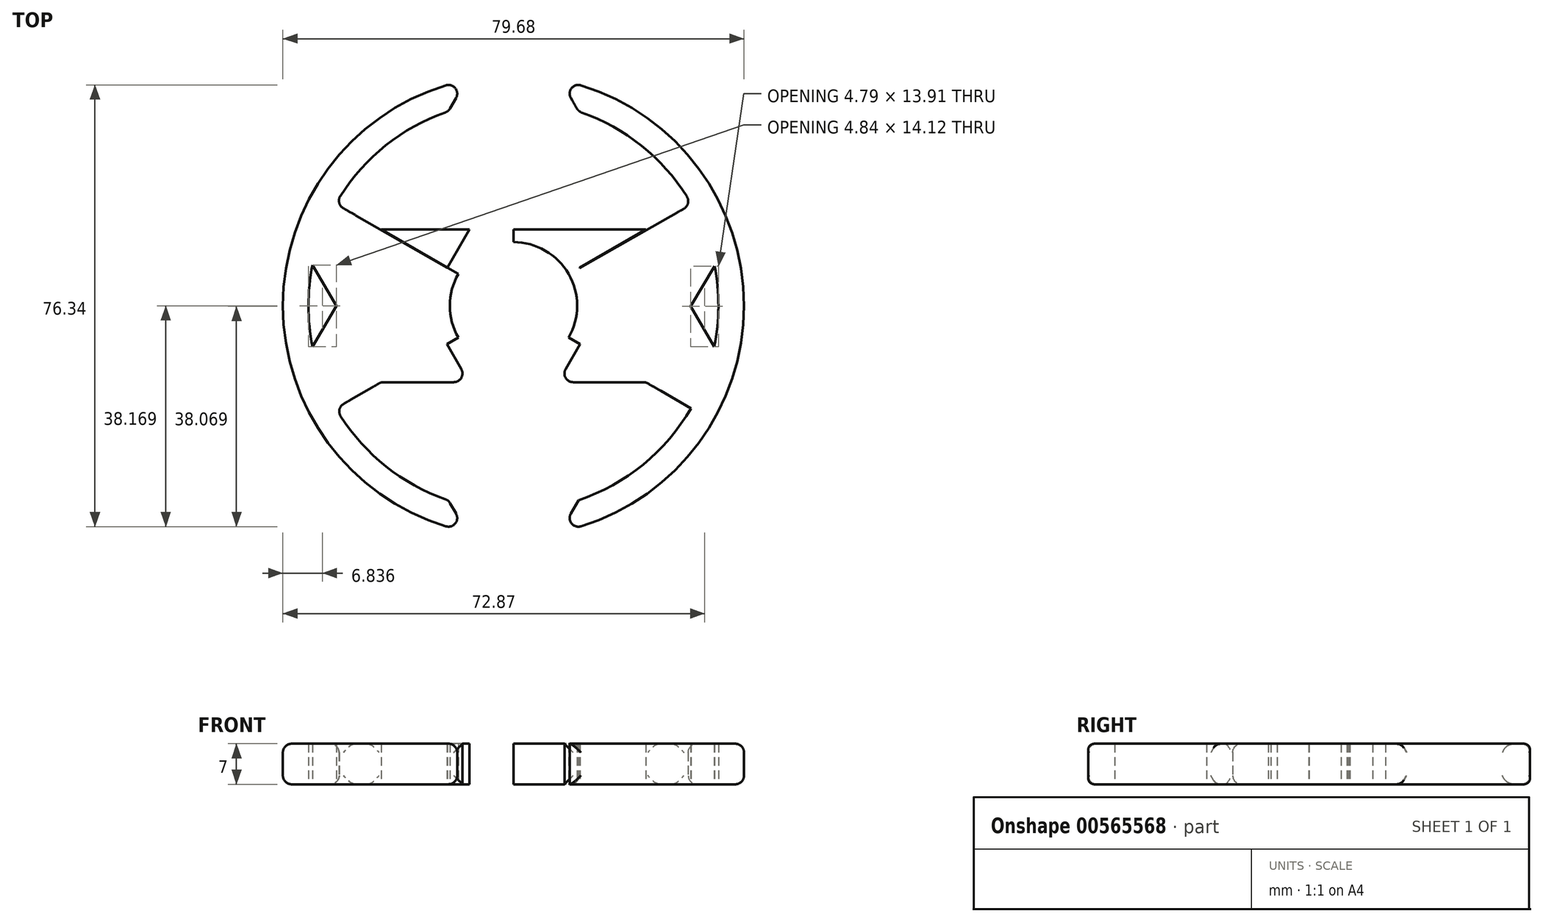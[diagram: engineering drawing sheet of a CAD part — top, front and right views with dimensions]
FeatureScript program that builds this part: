
annotation { "Feature Type Name" : "Feature", "Feature Type Description" : "" }
export const myFeature = defineFeature(function(context is Context, id is Id, definition is map)
    precondition{}
    {
        {
            var Q0;
            Q0=qCreatedBy(makeId("Top.planeOp"),FACE);
            var sketch = newSketch(context, id + "F0", { "sketchPlane" : qUnion([Q0])});
            skCircle(sketch, "E0", {"center": v(0, 0) * mm, "radius": 11 * mm});
            skCircle(sketch, "E1", {"center": v(0, 0) * mm, "radius": 26.4 * mm});
            skLineSegment(sketch, "E2", {"start": v(0, 0) * mm, "end": v(0, 26.4) * mm});
            skLineSegment(sketch, "E3", {"start": v(0, 0) * mm, "end": v(22.86, -13.2) * mm});
            skLineSegment(sketch, "E4", {"start": v(0, 0) * mm, "end": v(-22.86, -13.2) * mm});
            skLineSegment(sketch, "E5", {"start": v(0, 26.4) * mm, "end": v(-22.86, -13.2) * mm});
            skLineSegment(sketch, "E6", {"start": v(-22.86, -13.2) * mm, "end": v(22.86, -13.2) * mm});
            skLineSegment(sketch, "E7", {"start": v(22.86, -13.2) * mm, "end": v(0, 26.4) * mm});
            skCircle(sketch, "E8", {"center": v(0, 0) * mm, "radius": 30.74 * mm});
            skCircle(sketch, "E9", {"center": v(0, 0) * mm, "radius": 35.42 * mm});
            skCircle(sketch, "E10", {"center": v(0, 0) * mm, "radius": 39.84 * mm});
            skCircle(sketch, "E11", {"center": v(0, 0) * mm, "radius": 43.95 * mm});
            skCircle(sketch, "E12", {"center": v(0, 0) * mm, "radius": 48.64 * mm});
            skCircle(sketch, "E13", {"center": v(0, 0) * mm, "radius": 53.34 * mm});
            skLineSegment(sketch, "E14", {"start": v(0, 0) * mm, "end": v(-46.19, -26.67) * mm});
            skLineSegment(sketch, "E15", {"start": v(0, 0) * mm, "end": v(46.19, -26.67) * mm});
            skLineSegment(sketch, "E16", {"start": v(0, 0) * mm, "end": v(0, 53.34) * mm});
            skLineSegment(sketch, "E17", {"start": v(0, 0) * mm, "end": v(0, -26.67) * mm});
            skLineSegment(sketch, "E18", {"start": v(0, 0) * mm, "end": v(22.86, 13.2) * mm});
            skLineSegment(sketch, "E19", {"start": v(0, 0) * mm, "end": v(-22.86, 13.2) * mm});
            skLineSegment(sketch, "E20", {"start": v(-22.86, 13.2) * mm, "end": v(0, -26.67) * mm});
            skLineSegment(sketch, "E21", {"start": v(22.86, 13.2) * mm, "end": v(0, -26.67) * mm});
            skLineSegment(sketch, "E22", {"start": v(-22.86, 13.2) * mm, "end": v(22.86, 13.2) * mm});
            skLineSegment(sketch, "E23", {"start": v(0, 0) * mm, "end": v(46.35, 26.4) * mm});
            skLineSegment(sketch, "E24", {"start": v(0, 0) * mm, "end": v(0, -53.34) * mm});
            skLineSegment(sketch, "E25", {"start": v(0, 0) * mm, "end": v(-46.03, 26.4) * mm});
            skLineSegment(sketch, "E26", {"start": v(-46.03, 26.4) * mm, "end": v(-22.86, -13.2) * mm});
            skLineSegment(sketch, "E27", {"start": v(-46.19, -26.67) * mm, "end": v(-22.86, 13.2) * mm});
            skLineSegment(sketch, "E28", {"start": v(-46.19, -26.67) * mm, "end": v(0, -26.67) * mm});
            skLineSegment(sketch, "E29", {"start": v(-22.86, -13.2) * mm, "end": v(0, -53.34) * mm});
            skLineSegment(sketch, "E30", {"start": v(22.86, -13.2) * mm, "end": v(0, -53.34) * mm});
            skLineSegment(sketch, "E31", {"start": v(46.19, -26.67) * mm, "end": v(0, -26.67) * mm});
            skLineSegment(sketch, "E32", {"start": v(22.86, 13.2) * mm, "end": v(46.19, -26.67) * mm});
            skLineSegment(sketch, "E33", {"start": v(46.35, 26.4) * mm, "end": v(22.86, -13.2) * mm});
            skLineSegment(sketch, "E34", {"start": v(0, 26.4) * mm, "end": v(46.35, 26.4) * mm});
            skLineSegment(sketch, "E35", {"start": v(0, 53.34) * mm, "end": v(22.86, 13.2) * mm});
            skLineSegment(sketch, "E36", {"start": v(0, 53.34) * mm, "end": v(-22.86, 13.2) * mm});
            skLineSegment(sketch, "E37", {"start": v(-46.03, 26.4) * mm, "end": v(0, 26.4) * mm});
            skSolve(sketch);
        }
        {
            var Q0;
            {var subQ5=sQuery(id+"F0.wireOp",EDGE,"E0");var subQ7=sQuery(id+"F0.wireOp",EDGE,"E25");var subQ9=makeQuery(id+"F0.imprint","INTERSECT",VERTEX,{"derivedFrom":[subQ5,subQ7]});Q0=makeQuery(id+"F0.imprint","IMPRINT",FACE,{"disambiguationData":[TD([[makeQuery(id+"F0.imprint","IMPRINT",EDGE,{"disambiguationData":[TD([[subQ9,-1.0]])],"derivedFrom":subQ5}),-1.0]])]});}
            var Q1;
            {var subQ5=sQuery(id+"F0.wireOp",EDGE,"E23");var subQ7=sQuery(id+"F0.wireOp",EDGE,"E0");var subQ9=makeQuery(id+"F0.imprint","INTERSECT",VERTEX,{"derivedFrom":[subQ7,subQ5]});Q1=makeQuery(id+"F0.imprint","IMPRINT",FACE,{"disambiguationData":[TD([[makeQuery(id+"F0.imprint","IMPRINT",EDGE,{"disambiguationData":[TD([[subQ9,1.0]])],"derivedFrom":subQ7}),-1.0]])]});}
            var Q2;
            {var subQ3=sQuery(id+"F0.wireOp",EDGE,"E14");var subQ5=sQuery(id+"F0.wireOp",EDGE,"E0");var subQ6=makeQuery(id+"F0.imprint","INTERSECT",VERTEX,{"derivedFrom":[subQ5,subQ3]});Q2=makeQuery(id+"F0.imprint","IMPRINT",FACE,{"disambiguationData":[TD([[makeQuery(id+"F0.imprint","IMPRINT",EDGE,{"disambiguationData":[TD([[subQ6,-1.0]])],"derivedFrom":subQ5}),-1.0]])]});}
            var Q3;
            {var subQ0=sQuery(id+"F0.wireOp",EDGE,"E18");var subQ1=sQuery(id+"F0.wireOp",EDGE,"E0");var subQ2=makeQuery(id+"F0.imprint","INTERSECT",VERTEX,{"derivedFrom":[subQ1,subQ0]});Q3=makeQuery(id+"F0.imprint","IMPRINT",FACE,{"disambiguationData":[TD([[makeQuery(id+"F0.imprint","IMPRINT",EDGE,{"disambiguationData":[TD([[subQ2,-1.0]])],"derivedFrom":subQ1}),-1.0]])]});}
            var Q4;
            {var subQ5=sQuery(id+"F0.wireOp",EDGE,"E0");var subQ7=sQuery(id+"F0.wireOp",EDGE,"E24");var subQ9=makeQuery(id+"F0.imprint","INTERSECT",VERTEX,{"derivedFrom":[subQ5,subQ7]});Q4=makeQuery(id+"F0.imprint","IMPRINT",FACE,{"disambiguationData":[TD([[makeQuery(id+"F0.imprint","IMPRINT",EDGE,{"disambiguationData":[TD([[subQ9,-1.0]])],"derivedFrom":subQ5}),-1.0]])]});}
            var Q5;
            {var subQ1=sQuery(id+"F0.wireOp",EDGE,"E0");var subQ5=sQuery(id+"F0.wireOp",EDGE,"E16");var subQ6=makeQuery(id+"F0.imprint","INTERSECT",VERTEX,{"derivedFrom":[subQ1,subQ5]});Q5=makeQuery(id+"F0.imprint","IMPRINT",FACE,{"disambiguationData":[TD([[makeQuery(id+"F0.imprint","IMPRINT",EDGE,{"disambiguationData":[TD([[subQ6,-1.0]])],"derivedFrom":subQ1}),-1.0]])]});}
            var Q6;
            {var subQ0=sQuery(id+"F0.wireOp",EDGE,"E25");var subQ1=sQuery(id+"F0.wireOp",EDGE,"E5");var subQ2=makeQuery(id+"F0.imprint","INTERSECT",VERTEX,{"derivedFrom":[subQ1,subQ0]});Q6=makeQuery(id+"F0.imprint","IMPRINT",FACE,{"disambiguationData":[TD([[makeQuery(id+"F0.imprint","IMPRINT",EDGE,{"disambiguationData":[TD([[subQ2,-1.0]])],"derivedFrom":subQ1}),-1.0]])]});}
            var Q7;
            {var subQ1=sQuery(id+"F0.wireOp",EDGE,"E5");var subQ3=sQuery(id+"F0.wireOp",EDGE,"E20");var subQ4=makeQuery(id+"F0.imprint","INTERSECT",VERTEX,{"derivedFrom":[subQ1,subQ3]});Q7=makeQuery(id+"F0.imprint","IMPRINT",FACE,{"disambiguationData":[TD([[makeQuery(id+"F0.imprint","IMPRINT",EDGE,{"disambiguationData":[TD([[subQ4,-1.0]])],"derivedFrom":subQ3}),-1.0]])]});}
            var Q8;
            {var subQ0=sQuery(id+"F0.wireOp",EDGE,"E5");var subQ5=sQuery(id+"F0.wireOp",EDGE,"E20");var subQ6=makeQuery(id+"F0.imprint","INTERSECT",VERTEX,{"derivedFrom":[subQ0,subQ5]});Q8=makeQuery(id+"F0.imprint","IMPRINT",FACE,{"disambiguationData":[TD([[makeQuery(id+"F0.imprint","IMPRINT",EDGE,{"disambiguationData":[TD([[subQ6,1.0]])],"derivedFrom":subQ5}),-1.0]])]});}
            var Q9;
            {var subQ0=sQuery(id+"F0.wireOp",EDGE,"E7");var subQ5=sQuery(id+"F0.wireOp",EDGE,"E21");var subQ6=makeQuery(id+"F0.imprint","INTERSECT",VERTEX,{"derivedFrom":[subQ0,subQ5]});Q9=makeQuery(id+"F0.imprint","IMPRINT",FACE,{"disambiguationData":[TD([[makeQuery(id+"F0.imprint","IMPRINT",EDGE,{"disambiguationData":[TD([[subQ6,1.0]])],"derivedFrom":subQ5}),1.0]])]});}
            var Q10;
            {var subQ0=sQuery(id+"F0.wireOp",EDGE,"E21");var subQ1=sQuery(id+"F0.wireOp",EDGE,"E7");var subQ2=makeQuery(id+"F0.imprint","INTERSECT",VERTEX,{"derivedFrom":[subQ1,subQ0]});Q10=makeQuery(id+"F0.imprint","IMPRINT",FACE,{"disambiguationData":[TD([[makeQuery(id+"F0.imprint","IMPRINT",EDGE,{"disambiguationData":[TD([[subQ2,-1.0]])],"derivedFrom":subQ1}),-1.0]])]});}
            var Q11;
            {var subQ1=sQuery(id+"F0.wireOp",EDGE,"E7");var subQ3=sQuery(id+"F0.wireOp",EDGE,"E21");var subQ4=makeQuery(id+"F0.imprint","INTERSECT",VERTEX,{"derivedFrom":[subQ1,subQ3]});Q11=makeQuery(id+"F0.imprint","IMPRINT",FACE,{"disambiguationData":[TD([[makeQuery(id+"F0.imprint","IMPRINT",EDGE,{"disambiguationData":[TD([[subQ4,-1.0]])],"derivedFrom":subQ3}),1.0]])]});}
            var Q12;
            {var subQ0=sQuery(id+"F0.wireOp",EDGE,"E22");var subQ1=sQuery(id+"F0.wireOp",EDGE,"E5");var subQ2=makeQuery(id+"F0.imprint","INTERSECT",VERTEX,{"derivedFrom":[subQ1,subQ0]});Q12=makeQuery(id+"F0.imprint","IMPRINT",FACE,{"disambiguationData":[TD([[makeQuery(id+"F0.imprint","IMPRINT",EDGE,{"disambiguationData":[TD([[subQ2,-1.0]])],"derivedFrom":subQ1}),-1.0]])]});}
            var Q13;
            {var subQ1=sQuery(id+"F0.wireOp",EDGE,"E6");var subQ3=sQuery(id+"F0.wireOp",EDGE,"E20");var subQ4=makeQuery(id+"F0.imprint","INTERSECT",VERTEX,{"derivedFrom":[subQ1,subQ3]});Q13=makeQuery(id+"F0.imprint","IMPRINT",FACE,{"disambiguationData":[TD([[makeQuery(id+"F0.imprint","IMPRINT",EDGE,{"disambiguationData":[TD([[subQ4,1.0]])],"derivedFrom":subQ3}),-1.0]])]});}
            var Q14;
            {var subQ1=sQuery(id+"F0.wireOp",EDGE,"E6");var subQ3=sQuery(id+"F0.wireOp",EDGE,"E21");var subQ4=makeQuery(id+"F0.imprint","INTERSECT",VERTEX,{"derivedFrom":[subQ1,subQ3]});Q14=makeQuery(id+"F0.imprint","IMPRINT",FACE,{"disambiguationData":[TD([[makeQuery(id+"F0.imprint","IMPRINT",EDGE,{"disambiguationData":[TD([[subQ4,1.0]])],"derivedFrom":subQ3}),1.0]])]});}
            var Q15;
            {var subQ0=sQuery(id+"F0.wireOp",EDGE,"E18");var subQ1=sQuery(id+"F0.wireOp",EDGE,"E7");var subQ2=makeQuery(id+"F0.imprint","INTERSECT",VERTEX,{"derivedFrom":[subQ1,subQ0]});Q15=makeQuery(id+"F0.imprint","IMPRINT",FACE,{"disambiguationData":[TD([[makeQuery(id+"F0.imprint","IMPRINT",EDGE,{"disambiguationData":[TD([[subQ2,-1.0]])],"derivedFrom":subQ1}),-1.0]])]});}
            var Q16;
            {var subQ0=sQuery(id+"F0.wireOp",EDGE,"E25");var subQ1=sQuery(id+"F0.wireOp",EDGE,"E8");var subQ2=makeQuery(id+"F0.imprint","INTERSECT",VERTEX,{"derivedFrom":[subQ1,subQ0]});Q16=makeQuery(id+"F0.imprint","IMPRINT",FACE,{"disambiguationData":[TD([[makeQuery(id+"F0.imprint","IMPRINT",EDGE,{"disambiguationData":[TD([[subQ2,-1.0]])],"derivedFrom":subQ1}),1.0]])]});}
            var Q17;
            {var subQ0=sQuery(id+"F0.wireOp",EDGE,"E27");var subQ1=sQuery(id+"F0.wireOp",EDGE,"E8");var subQ2=makeQuery(id+"F0.imprint","INTERSECT",VERTEX,{"derivedFrom":[subQ1,subQ0]});Q17=makeQuery(id+"F0.imprint","IMPRINT",FACE,{"disambiguationData":[TD([[makeQuery(id+"F0.imprint","IMPRINT",EDGE,{"disambiguationData":[TD([[subQ2,-1.0]])],"derivedFrom":subQ1}),1.0]])]});}
            var Q18;
            {var subQ1=sQuery(id+"F0.wireOp",EDGE,"E1");var subQ3=sQuery(id+"F0.wireOp",EDGE,"E25");var subQ4=makeQuery(id+"F0.imprint","INTERSECT",VERTEX,{"derivedFrom":[subQ1,subQ3]});Q18=makeQuery(id+"F0.imprint","IMPRINT",FACE,{"disambiguationData":[TD([[makeQuery(id+"F0.imprint","IMPRINT",EDGE,{"disambiguationData":[TD([[subQ4,-1.0]])],"derivedFrom":subQ3}),1.0]])]});}
            var Q19;
            {var subQ0=sQuery(id+"F0.wireOp",EDGE,"E23");var subQ1=sQuery(id+"F0.wireOp",EDGE,"E8");var subQ2=makeQuery(id+"F0.imprint","INTERSECT",VERTEX,{"derivedFrom":[subQ1,subQ0]});Q19=makeQuery(id+"F0.imprint","IMPRINT",FACE,{"disambiguationData":[TD([[makeQuery(id+"F0.imprint","IMPRINT",EDGE,{"disambiguationData":[TD([[subQ2,1.0]])],"derivedFrom":subQ1}),1.0]])]});}
            var Q20;
            {var subQ1=sQuery(id+"F0.wireOp",EDGE,"E1");var subQ3=sQuery(id+"F0.wireOp",EDGE,"E23");var subQ4=makeQuery(id+"F0.imprint","INTERSECT",VERTEX,{"derivedFrom":[subQ1,subQ3]});Q20=makeQuery(id+"F0.imprint","IMPRINT",FACE,{"disambiguationData":[TD([[makeQuery(id+"F0.imprint","IMPRINT",EDGE,{"disambiguationData":[TD([[subQ4,-1.0]])],"derivedFrom":subQ3}),-1.0]])]});}
            var Q21;
            {var subQ0=sQuery(id+"F0.wireOp",EDGE,"E15");var subQ1=sQuery(id+"F0.wireOp",EDGE,"E8");var subQ2=makeQuery(id+"F0.imprint","INTERSECT",VERTEX,{"derivedFrom":[subQ1,subQ0]});Q21=makeQuery(id+"F0.imprint","IMPRINT",FACE,{"disambiguationData":[TD([[makeQuery(id+"F0.imprint","IMPRINT",EDGE,{"disambiguationData":[TD([[subQ2,-1.0]])],"derivedFrom":subQ1}),1.0]])]});}
            var Q22;
            {var subQ0=sQuery(id+"F0.wireOp",EDGE,"E23");var subQ1=sQuery(id+"F0.wireOp",EDGE,"E8");var subQ2=makeQuery(id+"F0.imprint","INTERSECT",VERTEX,{"derivedFrom":[subQ1,subQ0]});Q22=makeQuery(id+"F0.imprint","IMPRINT",FACE,{"disambiguationData":[TD([[makeQuery(id+"F0.imprint","IMPRINT",EDGE,{"disambiguationData":[TD([[subQ2,1.0]])],"derivedFrom":subQ1}),-1.0]])]});}
            var Q23;
            {var subQ0=sQuery(id+"F0.wireOp",EDGE,"E23");var subQ1=sQuery(id+"F0.wireOp",EDGE,"E9");var subQ2=makeQuery(id+"F0.imprint","INTERSECT",VERTEX,{"derivedFrom":[subQ1,subQ0]});Q23=makeQuery(id+"F0.imprint","IMPRINT",FACE,{"disambiguationData":[TD([[makeQuery(id+"F0.imprint","IMPRINT",EDGE,{"disambiguationData":[TD([[subQ2,1.0]])],"derivedFrom":subQ1}),-1.0]])]});}
            var Q24;
            {var subQ0=sQuery(id+"F0.wireOp",EDGE,"E15");var subQ1=sQuery(id+"F0.wireOp",EDGE,"E9");var subQ2=makeQuery(id+"F0.imprint","INTERSECT",VERTEX,{"derivedFrom":[subQ1,subQ0]});Q24=makeQuery(id+"F0.imprint","IMPRINT",FACE,{"disambiguationData":[TD([[makeQuery(id+"F0.imprint","IMPRINT",EDGE,{"disambiguationData":[TD([[subQ2,-1.0]])],"derivedFrom":subQ1}),-1.0]])]});}
            var Q25;
            {var subQ0=sQuery(id+"F0.wireOp",EDGE,"E15");var subQ1=sQuery(id+"F0.wireOp",EDGE,"E8");var subQ2=makeQuery(id+"F0.imprint","INTERSECT",VERTEX,{"derivedFrom":[subQ1,subQ0]});Q25=makeQuery(id+"F0.imprint","IMPRINT",FACE,{"disambiguationData":[TD([[makeQuery(id+"F0.imprint","IMPRINT",EDGE,{"disambiguationData":[TD([[subQ2,-1.0]])],"derivedFrom":subQ1}),-1.0]])]});}
            var Q26;
            {var subQ0=sQuery(id+"F0.wireOp",EDGE,"E27");var subQ1=sQuery(id+"F0.wireOp",EDGE,"E8");var subQ2=makeQuery(id+"F0.imprint","INTERSECT",VERTEX,{"derivedFrom":[subQ1,subQ0]});Q26=makeQuery(id+"F0.imprint","IMPRINT",FACE,{"disambiguationData":[TD([[makeQuery(id+"F0.imprint","IMPRINT",EDGE,{"disambiguationData":[TD([[subQ2,-1.0]])],"derivedFrom":subQ1}),-1.0]])]});}
            var Q27;
            {var subQ0=sQuery(id+"F0.wireOp",EDGE,"E27");var subQ1=sQuery(id+"F0.wireOp",EDGE,"E9");var subQ2=makeQuery(id+"F0.imprint","INTERSECT",VERTEX,{"derivedFrom":[subQ1,subQ0]});Q27=makeQuery(id+"F0.imprint","IMPRINT",FACE,{"disambiguationData":[TD([[makeQuery(id+"F0.imprint","IMPRINT",EDGE,{"disambiguationData":[TD([[subQ2,-1.0]])],"derivedFrom":subQ1}),-1.0]])]});}
            var Q28;
            {var subQ0=sQuery(id+"F0.wireOp",EDGE,"E25");var subQ1=sQuery(id+"F0.wireOp",EDGE,"E9");var subQ2=makeQuery(id+"F0.imprint","INTERSECT",VERTEX,{"derivedFrom":[subQ1,subQ0]});Q28=makeQuery(id+"F0.imprint","IMPRINT",FACE,{"disambiguationData":[TD([[makeQuery(id+"F0.imprint","IMPRINT",EDGE,{"disambiguationData":[TD([[subQ2,-1.0]])],"derivedFrom":subQ1}),-1.0]])]});}
            var Q29;
            {var subQ0=sQuery(id+"F0.wireOp",EDGE,"E25");var subQ1=sQuery(id+"F0.wireOp",EDGE,"E8");var subQ2=makeQuery(id+"F0.imprint","INTERSECT",VERTEX,{"derivedFrom":[subQ1,subQ0]});Q29=makeQuery(id+"F0.imprint","IMPRINT",FACE,{"disambiguationData":[TD([[makeQuery(id+"F0.imprint","IMPRINT",EDGE,{"disambiguationData":[TD([[subQ2,-1.0]])],"derivedFrom":subQ1}),-1.0]])]});}
            var Q30;
            {var subQ0=sQuery(id+"F0.wireOp",EDGE,"E37");var subQ1=sQuery(id+"F0.wireOp",EDGE,"E9");var subQ2=makeQuery(id+"F0.imprint","INTERSECT",VERTEX,{"derivedFrom":[subQ1,subQ0]});Q30=makeQuery(id+"F0.imprint","IMPRINT",FACE,{"disambiguationData":[TD([[makeQuery(id+"F0.imprint","IMPRINT",EDGE,{"disambiguationData":[TD([[subQ2,-1.0]])],"derivedFrom":subQ1}),-1.0]])]});}
            var Q31;
            {var subQ0=sQuery(id+"F0.wireOp",EDGE,"E31");var subQ1=sQuery(id+"F0.wireOp",EDGE,"E9");var subQ2=makeQuery(id+"F0.imprint","INTERSECT",VERTEX,{"derivedFrom":[subQ1,subQ0]});Q31=makeQuery(id+"F0.imprint","IMPRINT",FACE,{"disambiguationData":[TD([[makeQuery(id+"F0.imprint","IMPRINT",EDGE,{"disambiguationData":[TD([[subQ2,-1.0]])],"derivedFrom":subQ1}),-1.0]])]});}
            var Q32;
            {var subQ0=sQuery(id+"F0.wireOp",EDGE,"E14");var subQ1=sQuery(id+"F0.wireOp",EDGE,"E9");var subQ2=makeQuery(id+"F0.imprint","INTERSECT",VERTEX,{"derivedFrom":[subQ1,subQ0]});Q32=makeQuery(id+"F0.imprint","IMPRINT",FACE,{"disambiguationData":[TD([[makeQuery(id+"F0.imprint","IMPRINT",EDGE,{"disambiguationData":[TD([[subQ2,-1.0]])],"derivedFrom":subQ1}),-1.0]])]});}
            var Q33;
            {var subQ0=sQuery(id+"F0.wireOp",EDGE,"E23");var subQ1=sQuery(id+"F0.wireOp",EDGE,"E9");var subQ2=makeQuery(id+"F0.imprint","INTERSECT",VERTEX,{"derivedFrom":[subQ1,subQ0]});Q33=makeQuery(id+"F0.imprint","IMPRINT",FACE,{"disambiguationData":[TD([[makeQuery(id+"F0.imprint","IMPRINT",EDGE,{"disambiguationData":[TD([[subQ2,-1.0]])],"derivedFrom":subQ1}),-1.0]])]});}
            var Q34;
            {var subQ0=sQuery(id+"F0.wireOp",EDGE,"E33");var subQ1=sQuery(id+"F0.wireOp",EDGE,"E9");var subQ2=makeQuery(id+"F0.imprint","INTERSECT",VERTEX,{"derivedFrom":[subQ1,subQ0]});Q34=makeQuery(id+"F0.imprint","IMPRINT",FACE,{"disambiguationData":[TD([[makeQuery(id+"F0.imprint","IMPRINT",EDGE,{"disambiguationData":[TD([[subQ2,1.0]])],"derivedFrom":subQ1}),-1.0]])]});}
            var Q35;
            {var subQ0=sQuery(id+"F0.wireOp",EDGE,"E26");var subQ1=sQuery(id+"F0.wireOp",EDGE,"E9");var subQ2=makeQuery(id+"F0.imprint","INTERSECT",VERTEX,{"derivedFrom":[subQ1,subQ0]});Q35=makeQuery(id+"F0.imprint","IMPRINT",FACE,{"disambiguationData":[TD([[makeQuery(id+"F0.imprint","IMPRINT",EDGE,{"disambiguationData":[TD([[subQ2,-1.0]])],"derivedFrom":subQ1}),-1.0]])]});}
            var Q36;
            {var subQ0=sQuery(id+"F0.wireOp",EDGE,"E28");var subQ1=sQuery(id+"F0.wireOp",EDGE,"E9");var subQ2=makeQuery(id+"F0.imprint","INTERSECT",VERTEX,{"derivedFrom":[subQ1,subQ0]});Q36=makeQuery(id+"F0.imprint","IMPRINT",FACE,{"disambiguationData":[TD([[makeQuery(id+"F0.imprint","IMPRINT",EDGE,{"disambiguationData":[TD([[subQ2,-1.0]])],"derivedFrom":subQ1}),-1.0]])]});}
            var Q37;
            {var subQ0=sQuery(id+"F0.wireOp",EDGE,"E30");var subQ1=sQuery(id+"F0.wireOp",EDGE,"E9");var subQ2=makeQuery(id+"F0.imprint","INTERSECT",VERTEX,{"derivedFrom":[subQ1,subQ0]});Q37=makeQuery(id+"F0.imprint","IMPRINT",FACE,{"disambiguationData":[TD([[makeQuery(id+"F0.imprint","IMPRINT",EDGE,{"disambiguationData":[TD([[subQ2,-1.0]])],"derivedFrom":subQ1}),-1.0]])]});}
            var Q38;
            {var subQ0=sQuery(id+"F0.wireOp",EDGE,"E34");var subQ1=sQuery(id+"F0.wireOp",EDGE,"E9");var subQ2=makeQuery(id+"F0.imprint","INTERSECT",VERTEX,{"derivedFrom":[subQ1,subQ0]});Q38=makeQuery(id+"F0.imprint","IMPRINT",FACE,{"disambiguationData":[TD([[makeQuery(id+"F0.imprint","IMPRINT",EDGE,{"disambiguationData":[TD([[subQ2,-1.0]])],"derivedFrom":subQ1}),-1.0]])]});}
            var Q39;
            {var subQ0=sQuery(id+"F0.wireOp",EDGE,"E36");var subQ1=sQuery(id+"F0.wireOp",EDGE,"E9");var subQ2=makeQuery(id+"F0.imprint","INTERSECT",VERTEX,{"derivedFrom":[subQ1,subQ0]});Q39=makeQuery(id+"F0.imprint","IMPRINT",FACE,{"disambiguationData":[TD([[makeQuery(id+"F0.imprint","IMPRINT",EDGE,{"disambiguationData":[TD([[subQ2,-1.0]])],"derivedFrom":subQ1}),-1.0]])]});}
            extrude(context, id + "F1", {"entities" : qUnion([Q0, Q1, Q2, Q3, Q4, Q5, Q6, Q7, Q8, Q9, Q10, Q11, Q12, Q13, Q14, Q15, Q16, Q17, Q18, Q19, Q20, Q21, Q22, Q23, Q24, Q25, Q26, Q27, Q28, Q29, Q30, Q31, Q32, Q33, Q34, Q35, Q36, Q37, Q38, Q39]), "depth" : 7 * mm, "offsetDistance" : 25.4 * mm});
        }
        {
            var Q0;
            {var subQ0=sQuery(id+"F0.wireOp",EDGE,"E10");var subQ1=makeQuery(id+"F0.imprint","INTERSECT",VERTEX,{"derivedFrom":[subQ0,sQuery(id+"F0.wireOp",EDGE,"E33")]});var subQ3=makeQuery(id+"F0.imprint","INTERSECT",VERTEX,{"derivedFrom":[subQ0,sQuery(id+"F0.wireOp",EDGE,"E15")]});var subQ4=makeQuery(id+"F0.imprint","INTERSECT",VERTEX,{"derivedFrom":[subQ0,sQuery(id+"F0.wireOp",EDGE,"E31")]});var subQ5=makeQuery(id+"F0.imprint","INTERSECT",VERTEX,{"derivedFrom":[subQ0,sQuery(id+"F0.wireOp",EDGE,"E34")]});var subQ6=makeQuery(id+"F0.imprint","INTERSECT",VERTEX,{"derivedFrom":[subQ0,sQuery(id+"F0.wireOp",EDGE,"E23")]});Q0=makeQuery(id+"F1.opExtrude","SWEPT_FACE",FACE,{"disambiguationData":[OSD([subQ0]),TDD([makeQuery(id+"F0.imprint","IMPRINT",EDGE,{"disambiguationData":[TD([[subQ6,1.0]])],"derivedFrom":subQ0}),makeQuery(id+"F0.imprint","IMPRINT",EDGE,{"disambiguationData":[TD([[subQ6,-1.0]])],"derivedFrom":subQ0}),makeQuery(id+"F0.imprint","IMPRINT",EDGE,{"disambiguationData":[TD([[subQ5,-1.0]])],"derivedFrom":subQ0}),makeQuery(id+"F0.imprint","IMPRINT",EDGE,{"disambiguationData":[TD([[makeQuery(id+"F0.imprint","INTERSECT",VERTEX,{"derivedFrom":[subQ0,sQuery(id+"F0.wireOp",EDGE,"E30")]}),-1.0]])],"derivedFrom":subQ0}),makeQuery(id+"F0.imprint","IMPRINT",EDGE,{"disambiguationData":[TD([[subQ4,-1.0]])],"derivedFrom":subQ0}),makeQuery(id+"F0.imprint","IMPRINT",EDGE,{"disambiguationData":[TD([[subQ3,-1.0]])],"derivedFrom":subQ0}),makeQuery(id+"F0.imprint","IMPRINT",EDGE,{"disambiguationData":[TD([[subQ1,1.0]])],"derivedFrom":subQ0})])]});}
            var Q1;
            {var subQ0=sQuery(id+"F0.wireOp",EDGE,"E10");var subQ1=makeQuery(id+"F0.imprint","INTERSECT",VERTEX,{"derivedFrom":[subQ0,sQuery(id+"F0.wireOp",EDGE,"E28")]});var subQ2=makeQuery(id+"F0.imprint","INTERSECT",VERTEX,{"derivedFrom":[subQ0,sQuery(id+"F0.wireOp",EDGE,"E14")]});var subQ3=makeQuery(id+"F0.imprint","INTERSECT",VERTEX,{"derivedFrom":[subQ0,sQuery(id+"F0.wireOp",EDGE,"E27")]});var subQ4=makeQuery(id+"F0.imprint","INTERSECT",VERTEX,{"derivedFrom":[subQ0,sQuery(id+"F0.wireOp",EDGE,"E26")]});var subQ5=makeQuery(id+"F0.imprint","INTERSECT",VERTEX,{"derivedFrom":[subQ0,sQuery(id+"F0.wireOp",EDGE,"E25")]});var subQ6=makeQuery(id+"F0.imprint","INTERSECT",VERTEX,{"derivedFrom":[subQ0,sQuery(id+"F0.wireOp",EDGE,"E37")]});Q1=makeQuery(id+"F1.opExtrude","SWEPT_FACE",FACE,{"disambiguationData":[OSD([subQ0]),TDD([makeQuery(id+"F0.imprint","IMPRINT",EDGE,{"disambiguationData":[TD([[makeQuery(id+"F0.imprint","INTERSECT",VERTEX,{"derivedFrom":[subQ0,sQuery(id+"F0.wireOp",EDGE,"E36")]}),-1.0]])],"derivedFrom":subQ0}),makeQuery(id+"F0.imprint","IMPRINT",EDGE,{"disambiguationData":[TD([[subQ6,-1.0]])],"derivedFrom":subQ0}),makeQuery(id+"F0.imprint","IMPRINT",EDGE,{"disambiguationData":[TD([[subQ5,-1.0]])],"derivedFrom":subQ0}),makeQuery(id+"F0.imprint","IMPRINT",EDGE,{"disambiguationData":[TD([[subQ4,-1.0]])],"derivedFrom":subQ0}),makeQuery(id+"F0.imprint","IMPRINT",EDGE,{"disambiguationData":[TD([[subQ3,-1.0]])],"derivedFrom":subQ0}),makeQuery(id+"F0.imprint","IMPRINT",EDGE,{"disambiguationData":[TD([[subQ2,-1.0]])],"derivedFrom":subQ0}),makeQuery(id+"F0.imprint","IMPRINT",EDGE,{"disambiguationData":[TD([[subQ1,-1.0]])],"derivedFrom":subQ0})])]});}
            var Q2;
            Q2=makeQuery(id+"F1.opExtrude","SWEPT_FACE",FACE,{"disambiguationData":[OSD([sQuery(id+"F0.wireOp",EDGE,"E6")])]});
            var Q3;
            {var subQ0=sQuery(id+"F0.wireOp",EDGE,"E9");var subQ1=makeQuery(id+"F0.imprint","INTERSECT",VERTEX,{"derivedFrom":[subQ0,sQuery(id+"F0.wireOp",EDGE,"E37")]});Q3=makeQuery(id+"F1.opExtrude","SWEPT_FACE",FACE,{"disambiguationData":[OSD([subQ0]),TDD([makeQuery(id+"F0.imprint","IMPRINT",EDGE,{"disambiguationData":[TD([[makeQuery(id+"F0.imprint","INTERSECT",VERTEX,{"derivedFrom":[subQ0,sQuery(id+"F0.wireOp",EDGE,"E36")]}),-1.0]])],"derivedFrom":subQ0}),makeQuery(id+"F0.imprint","IMPRINT",EDGE,{"disambiguationData":[TD([[subQ1,-1.0]])],"derivedFrom":subQ0})])]});}
            var Q4;
            {var subQ0=sQuery(id+"F0.wireOp",EDGE,"E9");var subQ1=makeQuery(id+"F0.imprint","INTERSECT",VERTEX,{"derivedFrom":[subQ0,sQuery(id+"F0.wireOp",EDGE,"E34")]});Q4=makeQuery(id+"F1.opExtrude","CAP_EDGE",EDGE,{"disambiguationData":[OSD([subQ0]),TDD([makeQuery(id+"F0.imprint","IMPRINT",EDGE,{"disambiguationData":[TD([[makeQuery(id+"F0.imprint","INTERSECT",VERTEX,{"derivedFrom":[subQ0,sQuery(id+"F0.wireOp",EDGE,"E23")]}),-1.0]])],"derivedFrom":subQ0}),makeQuery(id+"F0.imprint","IMPRINT",EDGE,{"disambiguationData":[TD([[subQ1,-1.0]])],"derivedFrom":subQ0})])],"isStart":true});}
            var Q5;
            {var subQ0=sQuery(id+"F0.wireOp",EDGE,"E9");var subQ1=makeQuery(id+"F0.imprint","INTERSECT",VERTEX,{"derivedFrom":[subQ0,sQuery(id+"F0.wireOp",EDGE,"E28")]});Q5=makeQuery(id+"F1.opExtrude","SWEPT_FACE",FACE,{"disambiguationData":[OSD([subQ0]),TDD([makeQuery(id+"F0.imprint","IMPRINT",EDGE,{"disambiguationData":[TD([[makeQuery(id+"F0.imprint","INTERSECT",VERTEX,{"derivedFrom":[subQ0,sQuery(id+"F0.wireOp",EDGE,"E14")]}),-1.0]])],"derivedFrom":subQ0}),makeQuery(id+"F0.imprint","IMPRINT",EDGE,{"disambiguationData":[TD([[subQ1,-1.0]])],"derivedFrom":subQ0})])]});}
            var Q6;
            Q6=makeQuery(id+"F1.opExtrude","SWEPT_FACE",FACE,{"disambiguationData":[OSD([sQuery(id+"F0.wireOp",EDGE,"E29")])]});
            var Q7;
            Q7=makeQuery(id+"F1.opExtrude","SWEPT_FACE",FACE,{"disambiguationData":[OSD([sQuery(id+"F0.wireOp",EDGE,"E36")])]});
            var Q8;
            Q8=makeQuery(id+"F1.opExtrude","SWEPT_EDGE",EDGE,{"disambiguationData":[OSD([sQuery(id+"F0.wireOp",EDGE,"E9"),sQuery(id+"F0.wireOp",EDGE,"E35")])]});
            var Q9;
            {var subQ0=sQuery(id+"F0.wireOp",EDGE,"E9");var subQ1=makeQuery(id+"F0.imprint","INTERSECT",VERTEX,{"derivedFrom":[subQ0,sQuery(id+"F0.wireOp",EDGE,"E34")]});Q9=makeQuery(id+"F1.opExtrude","SWEPT_FACE",FACE,{"disambiguationData":[OSD([subQ0]),TDD([makeQuery(id+"F0.imprint","IMPRINT",EDGE,{"disambiguationData":[TD([[makeQuery(id+"F0.imprint","INTERSECT",VERTEX,{"derivedFrom":[subQ0,sQuery(id+"F0.wireOp",EDGE,"E23")]}),-1.0]])],"derivedFrom":subQ0}),makeQuery(id+"F0.imprint","IMPRINT",EDGE,{"disambiguationData":[TD([[subQ1,-1.0]])],"derivedFrom":subQ0})])]});}
            fillet(context, id + "F2", {"entities" : qUnion([Q0, Q1, Q2, Q3, Q4, Q5, Q6, Q7, Q8, Q9]), "radius" : 1.5 * mm, "tangentPropagation" : true, "allowEdgeOverflow" : false});
        }
    });
